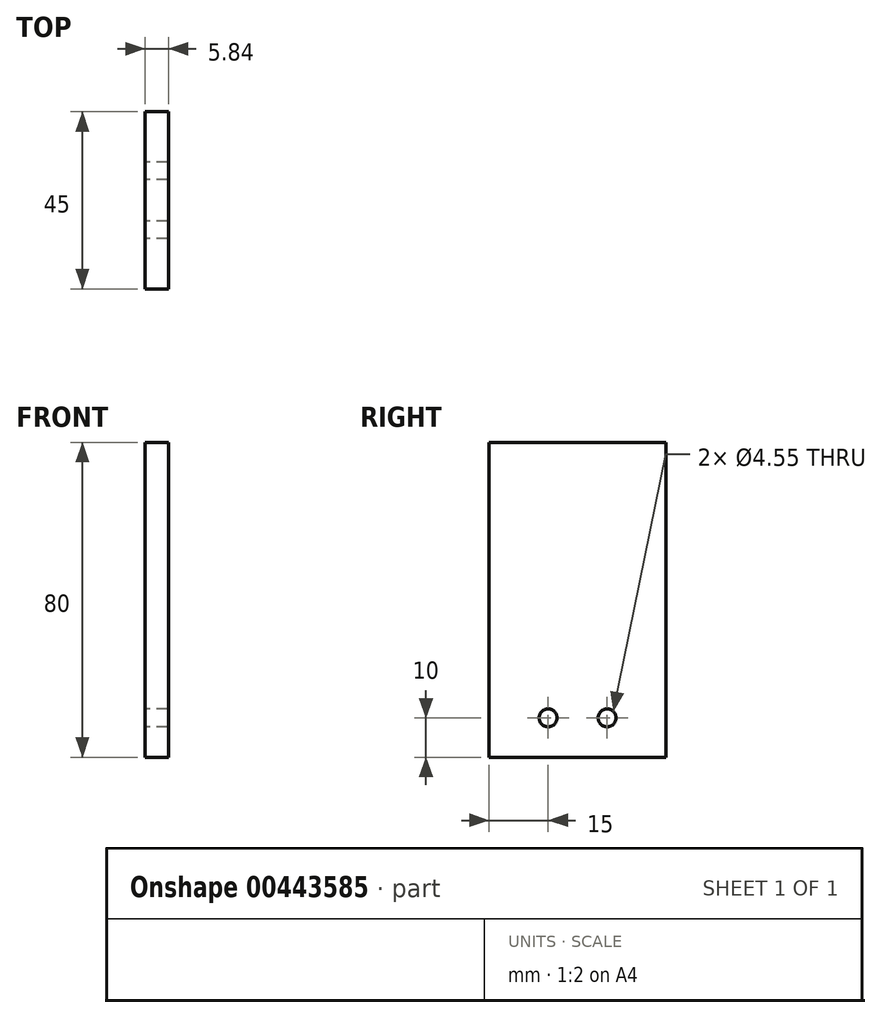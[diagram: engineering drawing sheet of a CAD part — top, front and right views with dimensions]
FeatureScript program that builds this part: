
annotation { "Feature Type Name" : "Feature", "Feature Type Description" : "" }
export const myFeature = defineFeature(function(context is Context, id is Id, definition is map)
    precondition{}
    {
        {
            var Q0;
            Q0=qCreatedBy(makeId("Right.planeOp"),FACE);
            var sketch = newSketch(context, id + "F0", { "sketchPlane" : qUnion([Q0])});
            skLineSegment(sketch, "E0.bottom", {"start": v(0, 0) * mm, "end": v(-45, 0) * mm});
            skLineSegment(sketch, "E0.top", {"start": v(0, 80) * mm, "end": v(-45, 80) * mm});
            skLineSegment(sketch, "E0.left", {"start": v(0, 0) * mm, "end": v(0, 80) * mm});
            skLineSegment(sketch, "E0.right", {"start": v(-45, 0) * mm, "end": v(-45, 80) * mm});
            skCircle(sketch, "E1", {"center": v(11955, 10) * mm, "radius": 6.6 * mm});
            skCircle(sketch, "E2", {"center": v(-15, 10) * mm, "radius": 2.27 * mm});
            skCircle(sketch, "E3", {"center": v(-30, 10) * mm, "radius": 2.27 * mm});
            skSolve(sketch);
        }
        {
            var Q0;
            Q0=makeQuery(id+"F0.imprint","IMPRINT",FACE,{"disambiguationData":[TD([[makeQuery(id+"F0.imprint","IMPRINT",EDGE,{"derivedFrom":sQuery(id+"F0.wireOp",EDGE,"E0.bottom")}),-1.0]])]});
            extrude(context, id + "F1", {"entities" : qUnion([Q0]), "depth" : 5.84 * mm});
        }
    });
